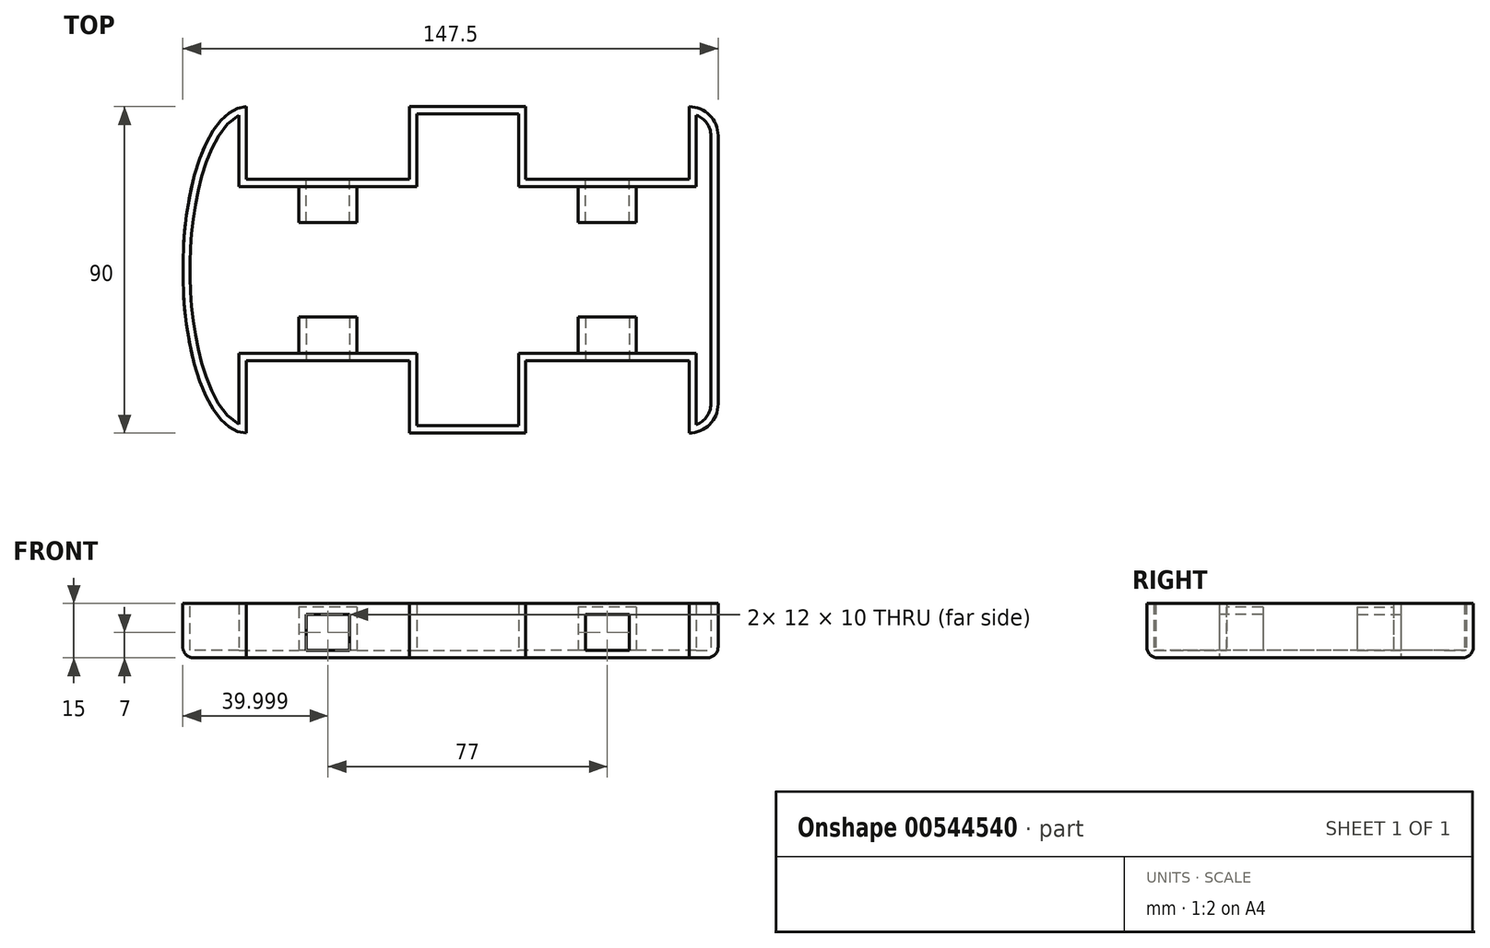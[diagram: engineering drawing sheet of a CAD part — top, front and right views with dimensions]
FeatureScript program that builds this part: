
annotation { "Feature Type Name" : "Feature", "Feature Type Description" : "" }
export const myFeature = defineFeature(function(context is Context, id is Id, definition is map)
    precondition{}
    {
        {
            var Q0;
            Q0=qCreatedBy(makeId("Top.planeOp"),FACE);
            var sketch = newSketch(context, id + "F0", { "sketchPlane" : qUnion([Q0])});
            skLineSegment(sketch, "E0.bottom", {"start": v(-27.96, 31.8) * mm, "end": v(4.04, 31.8) * mm});
            skLineSegment(sketch, "E0.top", {"start": v(-27.96, -58.2) * mm, "end": v(4.04, -58.2) * mm});
            skLineSegment(sketch, "E0.right", {"start": v(57.04, 23.8) * mm, "end": v(57.04, -50.2) * mm});
            skEllipticalArc(sketch, "E1", {});
            skPoint(sketch, "E2.visualSharp", {"position": v(57.04, 31.8) * mm});
            skArc(sketch, "E2.filletArc", {"start": v(57.04, 23.8) * mm, "mid": v(54.7, 29.46) * mm, "end": v(49.04, 31.8) * mm});
            skPoint(sketch, "E3.visualSharp", {"position": v(57.04, -58.2) * mm});
            skArc(sketch, "E3.filletArc", {"start": v(49.04, -58.2) * mm, "mid": v(54.7, -55.86) * mm, "end": v(57.04, -50.2) * mm});
            skLineSegment(sketch, "E4.top", {"start": v(-72.96, 11.8) * mm, "end": v(-27.96, 11.8) * mm});
            skLineSegment(sketch, "E4.left", {"start": v(-72.96, 31.8) * mm, "end": v(-72.96, 11.8) * mm});
            skLineSegment(sketch, "E4.right", {"start": v(-27.96, 31.8) * mm, "end": v(-27.96, 11.8) * mm});
            skLineSegment(sketch, "E5.top", {"start": v(49.04, 11.8) * mm, "end": v(4.04, 11.8) * mm});
            skLineSegment(sketch, "E5.left", {"start": v(49.04, 31.8) * mm, "end": v(49.04, 11.8) * mm});
            skLineSegment(sketch, "E5.right", {"start": v(4.04, 31.8) * mm, "end": v(4.04, 11.8) * mm});
            skLineSegment(sketch, "E6.top", {"start": v(-72.96, -38.2) * mm, "end": v(-27.96, -38.2) * mm});
            skLineSegment(sketch, "E6.left", {"start": v(-72.96, -58.2) * mm, "end": v(-72.96, -38.2) * mm});
            skLineSegment(sketch, "E6.right", {"start": v(-27.96, -58.2) * mm, "end": v(-27.96, -38.2) * mm});
            skLineSegment(sketch, "E7.top", {"start": v(49.04, -38.2) * mm, "end": v(4.04, -38.2) * mm});
            skLineSegment(sketch, "E7.left", {"start": v(49.04, -58.2) * mm, "end": v(49.04, -38.2) * mm});
            skLineSegment(sketch, "E7.right", {"start": v(4.04, -58.2) * mm, "end": v(4.04, -38.2) * mm});
            const initialGuessF0  = {"E1": [-0.07296122312545783, -0.013199719845870844, 0, 1, 0.045, 0.017502275273123383, 0, 3.141592653589793]};
            skSetInitialGuess(sketch, initialGuessF0);
            skSolve(sketch);
        }
        {
            var Q0;
            Q0=makeQuery(id+"F0.imprint","IMPRINT",FACE,{"disambiguationData":[TD([[makeQuery(id+"F0.imprint","IMPRINT",EDGE,{"derivedFrom":sQuery(id+"F0.wireOp",EDGE,"E0.bottom")}),-1.0]])]});
            extrude(context, id + "F1", {"entities" : qUnion([Q0]), "depth" : 15 * mm, "offsetDistance" : 25 * mm});
        }
        {
            var Q0;
            Q0=makeQuery(id+"F1.opExtrude","CAP_FACE",FACE,{"disambiguationData":[OSD([sQuery(id+"F0.wireOp",EDGE,"E0.bottom"),sQuery(id+"F0.wireOp",EDGE,"E0.top"),sQuery(id+"F0.wireOp",EDGE,"E0.right"),sQuery(id+"F0.wireOp",EDGE,"E1"),sQuery(id+"F0.wireOp",EDGE,"E2.filletArc"),sQuery(id+"F0.wireOp",EDGE,"E3.filletArc"),sQuery(id+"F0.wireOp",EDGE,"E4.top"),sQuery(id+"F0.wireOp",EDGE,"E4.left"),sQuery(id+"F0.wireOp",EDGE,"E4.right"),sQuery(id+"F0.wireOp",EDGE,"E5.top"),sQuery(id+"F0.wireOp",EDGE,"E5.left"),sQuery(id+"F0.wireOp",EDGE,"E5.right"),sQuery(id+"F0.wireOp",EDGE,"E6.top"),sQuery(id+"F0.wireOp",EDGE,"E6.left"),sQuery(id+"F0.wireOp",EDGE,"E6.right"),sQuery(id+"F0.wireOp",EDGE,"E7.top"),sQuery(id+"F0.wireOp",EDGE,"E7.left"),sQuery(id+"F0.wireOp",EDGE,"E7.right")])],"isStart":false});
            shell(context, id + "F2", {"entities" : qUnion([Q0]), "thickness" : 2 * mm});
        }
        {
            var Q0;
            Q0=makeQuery(id+"F1.opExtrude","CAP_EDGE",EDGE,{"disambiguationData":[OSD([sQuery(id+"F0.wireOp",EDGE,"E1")])],"isStart":true});
            var Q1;
            Q1=makeQuery(id+"F1.opExtrude","CAP_EDGE",EDGE,{"disambiguationData":[OSD([sQuery(id+"F0.wireOp",EDGE,"E0.top")])],"isStart":true});
            var Q2;
            Q2=makeQuery(id+"F1.opExtrude","CAP_EDGE",EDGE,{"disambiguationData":[OSD([sQuery(id+"F0.wireOp",EDGE,"E0.bottom")])],"isStart":true});
            var Q3;
            Q3=makeQuery(id+"F1.opExtrude","CAP_EDGE",EDGE,{"disambiguationData":[OSD([sQuery(id+"F0.wireOp",EDGE,"E0.right")])],"isStart":true});
            fillet(context, id + "F3", {"entities" : qUnion([Q0, Q1, Q2, Q3]), "radius" : 3 * mm, "tangentPropagation" : true, "allowEdgeOverflow" : false});
        }
        {
            var Q0;
            Q0=makeQuery(id+"F1.opExtrude","SWEPT_FACE",FACE,{"disambiguationData":[OSD([sQuery(id+"F0.wireOp",EDGE,"E6.top")])]});
            var sketch = newSketch(context, id + "F4", { "sketchPlane" : qUnion([Q0])});
            skLineSegment(sketch, "E8.bottom", {"start": v(-56.46, 12) * mm, "end": v(-44.46, 12) * mm});
            skLineSegment(sketch, "E8.top", {"start": v(-56.46, 2) * mm, "end": v(-44.46, 2) * mm});
            skLineSegment(sketch, "E8.left", {"start": v(-56.46, 12) * mm, "end": v(-56.46, 2) * mm});
            skLineSegment(sketch, "E8.right", {"start": v(-44.46, 12) * mm, "end": v(-44.46, 2) * mm});
            skSolve(sketch);
        }
        {
            var Q0;
            Q0=makeQuery(id+"F4.imprint","IMPRINT",FACE,{"disambiguationData":[TD([[makeQuery(id+"F4.imprint","IMPRINT",EDGE,{"derivedFrom":sQuery(id+"F4.wireOp",EDGE,"E8.bottom")}),1.0]])]});
            var sketch = newSketch(context, id + "F5", { "sketchPlane" : qUnion([Q0])});
            skLineSegment(sketch, "E9.bottom", {"start": v(-58.46, 14) * mm, "end": v(-42.46, 14) * mm});
            skLineSegment(sketch, "E9.top", {"start": v(-58.46, 2) * mm, "end": v(-42.46, 2) * mm});
            skLineSegment(sketch, "E9.left", {"start": v(-58.46, 14) * mm, "end": v(-58.46, 2) * mm});
            skLineSegment(sketch, "E9.right", {"start": v(-42.46, 14) * mm, "end": v(-42.46, 2) * mm});
            skSolve(sketch);
        }
        {
            var Q0;
            Q0=qSketchRegion(id+"F5",true);
            extrude(context, id + "F6", {"entities" : qUnion([Q0]), "operationType" : NewBodyOperationType.ADD, "oppositeDirection" : true, "depth" : 12 * mm, "offsetDistance" : 25 * mm});
        }
        {
            var Q0;
            Q0=qSketchRegion(id+"F4",true);
            extrude(context, id + "F7", {"entities" : qUnion([Q0]), "operationType" : NewBodyOperationType.REMOVE, "oppositeDirection" : true, "depth" : 12 * mm, "offsetDistance" : 25 * mm});
        }
        {
            var Q0;
            Q0=makeQuery(id+"F1.opExtrude","SWEPT_FACE",FACE,{"disambiguationData":[OSD([sQuery(id+"F0.wireOp",EDGE,"E4.top")])]});
            var sketch = newSketch(context, id + "F8", { "sketchPlane" : qUnion([Q0])});
            skLineSegment(sketch, "E10.bottom", {"start": v(42.46, 14) * mm, "end": v(58.46, 14) * mm});
            skLineSegment(sketch, "E10.top", {"start": v(42.46, 2) * mm, "end": v(58.46, 2) * mm});
            skLineSegment(sketch, "E10.left", {"start": v(42.46, 14) * mm, "end": v(42.46, 2) * mm});
            skLineSegment(sketch, "E10.right", {"start": v(58.46, 14) * mm, "end": v(58.46, 2) * mm});
            skSolve(sketch);
        }
        {
            var Q0;
            Q0=makeQuery(id+"F8.imprint","IMPRINT",FACE,{"disambiguationData":[TD([[makeQuery(id+"F8.imprint","IMPRINT",EDGE,{"derivedFrom":sQuery(id+"F8.wireOp",EDGE,"E10.bottom")}),1.0]])]});
            var sketch = newSketch(context, id + "F9", { "sketchPlane" : qUnion([Q0])});
            skLineSegment(sketch, "E11.bottom", {"start": v(44.46, 12) * mm, "end": v(56.46, 12) * mm});
            skLineSegment(sketch, "E11.top", {"start": v(44.46, 2) * mm, "end": v(56.46, 2) * mm});
            skLineSegment(sketch, "E11.left", {"start": v(44.46, 12) * mm, "end": v(44.46, 2) * mm});
            skLineSegment(sketch, "E11.right", {"start": v(56.46, 12) * mm, "end": v(56.46, 2) * mm});
            skSolve(sketch);
        }
        {
            var Q0;
            Q0=qSketchRegion(id+"F8",true);
            extrude(context, id + "F10", {"entities" : qUnion([Q0]), "operationType" : NewBodyOperationType.ADD, "oppositeDirection" : true, "depth" : 12 * mm, "offsetDistance" : 25 * mm});
        }
        {
            var Q0;
            Q0=qSketchRegion(id+"F9",true);
            extrude(context, id + "F11", {"entities" : qUnion([Q0]), "operationType" : NewBodyOperationType.REMOVE, "oppositeDirection" : true, "depth" : 12 * mm, "offsetDistance" : 25 * mm});
        }
        {
            var Q0;
            Q0=makeQuery(id+"F1.opExtrude","SWEPT_FACE",FACE,{"disambiguationData":[OSD([sQuery(id+"F0.wireOp",EDGE,"E7.top")])]});
            var sketch = newSketch(context, id + "F12", { "sketchPlane" : qUnion([Q0])});
            skLineSegment(sketch, "E12.bottom", {"start": v(18.54, 14) * mm, "end": v(34.54, 14) * mm});
            skLineSegment(sketch, "E12.top", {"start": v(18.54, 2) * mm, "end": v(34.54, 2) * mm});
            skLineSegment(sketch, "E12.left", {"start": v(18.54, 14) * mm, "end": v(18.54, 2) * mm});
            skLineSegment(sketch, "E12.right", {"start": v(34.54, 14) * mm, "end": v(34.54, 2) * mm});
            skSolve(sketch);
        }
        {
            var Q0;
            Q0=makeQuery(id+"F12.imprint","IMPRINT",FACE,{"disambiguationData":[TD([[makeQuery(id+"F12.imprint","IMPRINT",EDGE,{"derivedFrom":sQuery(id+"F12.wireOp",EDGE,"E12.bottom")}),1.0]])]});
            var sketch = newSketch(context, id + "F13", { "sketchPlane" : qUnion([Q0])});
            skLineSegment(sketch, "E13.bottom", {"start": v(20.54, 12) * mm, "end": v(32.54, 12) * mm});
            skLineSegment(sketch, "E13.top", {"start": v(20.54, 2) * mm, "end": v(32.54, 2) * mm});
            skLineSegment(sketch, "E13.left", {"start": v(20.54, 12) * mm, "end": v(20.54, 2) * mm});
            skLineSegment(sketch, "E13.right", {"start": v(32.54, 12) * mm, "end": v(32.54, 2) * mm});
            skSolve(sketch);
        }
        {
            var Q0;
            Q0=qSketchRegion(id+"F12",true);
            extrude(context, id + "F14", {"entities" : qUnion([Q0]), "operationType" : NewBodyOperationType.ADD, "oppositeDirection" : true, "depth" : 12 * mm, "offsetDistance" : 25 * mm});
        }
        {
            var Q0;
            Q0=qSketchRegion(id+"F13",true);
            extrude(context, id + "F15", {"entities" : qUnion([Q0]), "operationType" : NewBodyOperationType.REMOVE, "oppositeDirection" : true, "depth" : 12 * mm, "offsetDistance" : 25 * mm});
        }
        {
            var Q0;
            Q0=makeQuery(id+"F1.opExtrude","SWEPT_FACE",FACE,{"disambiguationData":[OSD([sQuery(id+"F0.wireOp",EDGE,"E5.top")])]});
            var sketch = newSketch(context, id + "F16", { "sketchPlane" : qUnion([Q0])});
            skLineSegment(sketch, "E14.bottom", {"start": v(-34.54, 14) * mm, "end": v(-18.54, 14) * mm});
            skLineSegment(sketch, "E14.top", {"start": v(-34.54, 2) * mm, "end": v(-18.54, 2) * mm});
            skLineSegment(sketch, "E14.left", {"start": v(-34.54, 14) * mm, "end": v(-34.54, 2) * mm});
            skLineSegment(sketch, "E14.right", {"start": v(-18.54, 14) * mm, "end": v(-18.54, 2) * mm});
            skSolve(sketch);
        }
        {
            var Q0;
            Q0=makeQuery(id+"F16.imprint","IMPRINT",FACE,{"disambiguationData":[TD([[makeQuery(id+"F16.imprint","IMPRINT",EDGE,{"derivedFrom":sQuery(id+"F16.wireOp",EDGE,"E14.bottom")}),1.0]])]});
            var sketch = newSketch(context, id + "F17", { "sketchPlane" : qUnion([Q0])});
            skLineSegment(sketch, "E15.bottom", {"start": v(-32.54, 12) * mm, "end": v(-20.54, 12) * mm});
            skLineSegment(sketch, "E15.top", {"start": v(-32.54, 2) * mm, "end": v(-20.54, 2) * mm});
            skLineSegment(sketch, "E15.left", {"start": v(-32.54, 12) * mm, "end": v(-32.54, 2) * mm});
            skLineSegment(sketch, "E15.right", {"start": v(-20.54, 12) * mm, "end": v(-20.54, 2) * mm});
            skSolve(sketch);
        }
        {
            var Q0;
            Q0=qSketchRegion(id+"F16",true);
            extrude(context, id + "F18", {"entities" : qUnion([Q0]), "operationType" : NewBodyOperationType.ADD, "oppositeDirection" : true, "depth" : 12 * mm, "offsetDistance" : 25 * mm});
        }
        {
            var Q0;
            Q0=makeQuery(id+"F17.imprint","IMPRINT",FACE,{"disambiguationData":[TD([[makeQuery(id+"F17.imprint","IMPRINT",EDGE,{"derivedFrom":sQuery(id+"F17.wireOp",EDGE,"E15.bottom")}),-1.0]])]});
            extrude(context, id + "F19", {"entities" : qUnion([Q0]), "operationType" : NewBodyOperationType.REMOVE, "oppositeDirection" : true, "depth" : 12 * mm, "offsetDistance" : 25 * mm});
        }
    });
